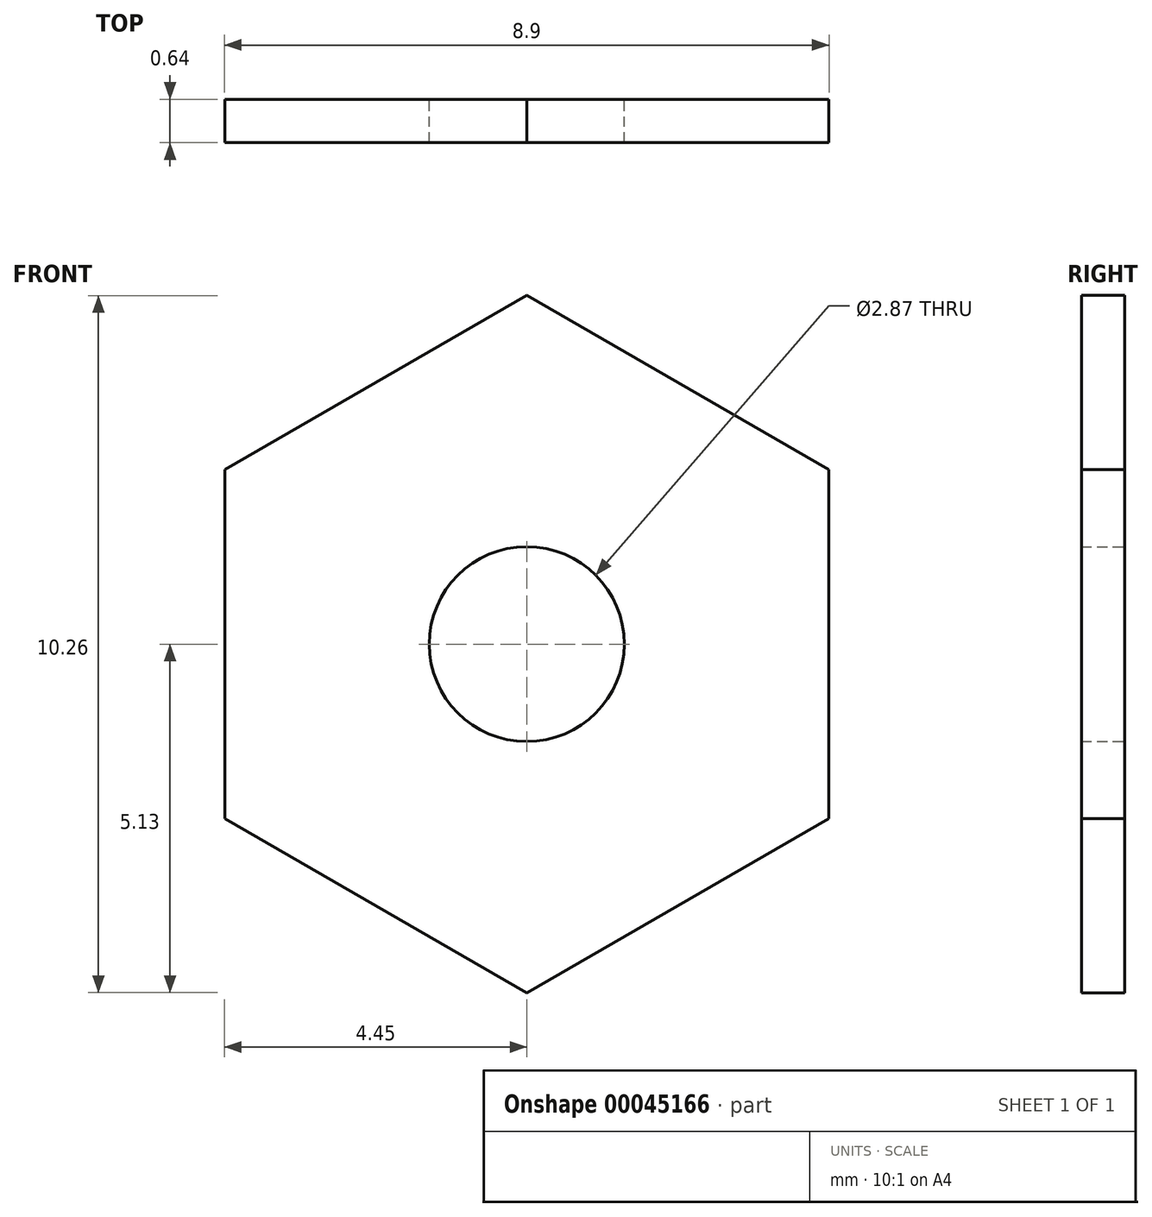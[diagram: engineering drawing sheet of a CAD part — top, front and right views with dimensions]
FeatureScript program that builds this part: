
annotation { "Feature Type Name" : "Feature", "Feature Type Description" : "" }
export const myFeature = defineFeature(function(context is Context, id is Id, definition is map)
    precondition{}
    {
        {
            var Q0;
            Q0=qCreatedBy(makeId("Front.planeOp"),FACE);
            var sketch = newSketch(context, id + "F0", { "sketchPlane" : qUnion([Q0])});
            skLineSegment(sketch, "E0", {"start": v(0, 0) * mm, "end": v(4.45, 0) * mm, "construction": true});
            skCircle(sketch, "E1.cCircle", {"center": v(0, 0) * mm, "radius": 4.45 * mm, "construction": true});
            skLineSegment(sketch, "E1.0", {"start": v(4.45, 2.57) * mm, "end": v(4.45, -2.57) * mm});
            skLineSegment(sketch, "E1.1", {"start": v(4.45, -2.57) * mm, "end": v(0, -5.13) * mm});
            skLineSegment(sketch, "E1.2", {"start": v(0, -5.13) * mm, "end": v(-4.45, -2.57) * mm});
            skLineSegment(sketch, "E1.3", {"start": v(-4.44, -2.57) * mm, "end": v(-4.45, 2.57) * mm});
            skLineSegment(sketch, "E1.4", {"start": v(-4.44, 2.57) * mm, "end": v(0, 5.13) * mm});
            skLineSegment(sketch, "E1.5", {"start": v(0, 5.13) * mm, "end": v(4.45, 2.57) * mm});
            skPoint(sketch, "E1.0.midPoint", {"position": v(4.45, 0) * mm});
            skLineSegment(sketch, "E2", {"start": v(0, 0) * mm, "end": v(1.44, 0) * mm});
            skPoint(sketch, "E3.0.midPoint", {"position": v(1.44, 0) * mm});
            skCircle(sketch, "E4", {"center": v(0, 0) * mm, "radius": 1.44 * mm});
            skSolve(sketch);
        }
        {
            var Q0;
            Q0=qSketchRegion(id+"F0",true);
            extrude(context, id + "F1", {"entities" : qUnion([Q0]), "depth" : 0.64 * mm});
        }
    });
